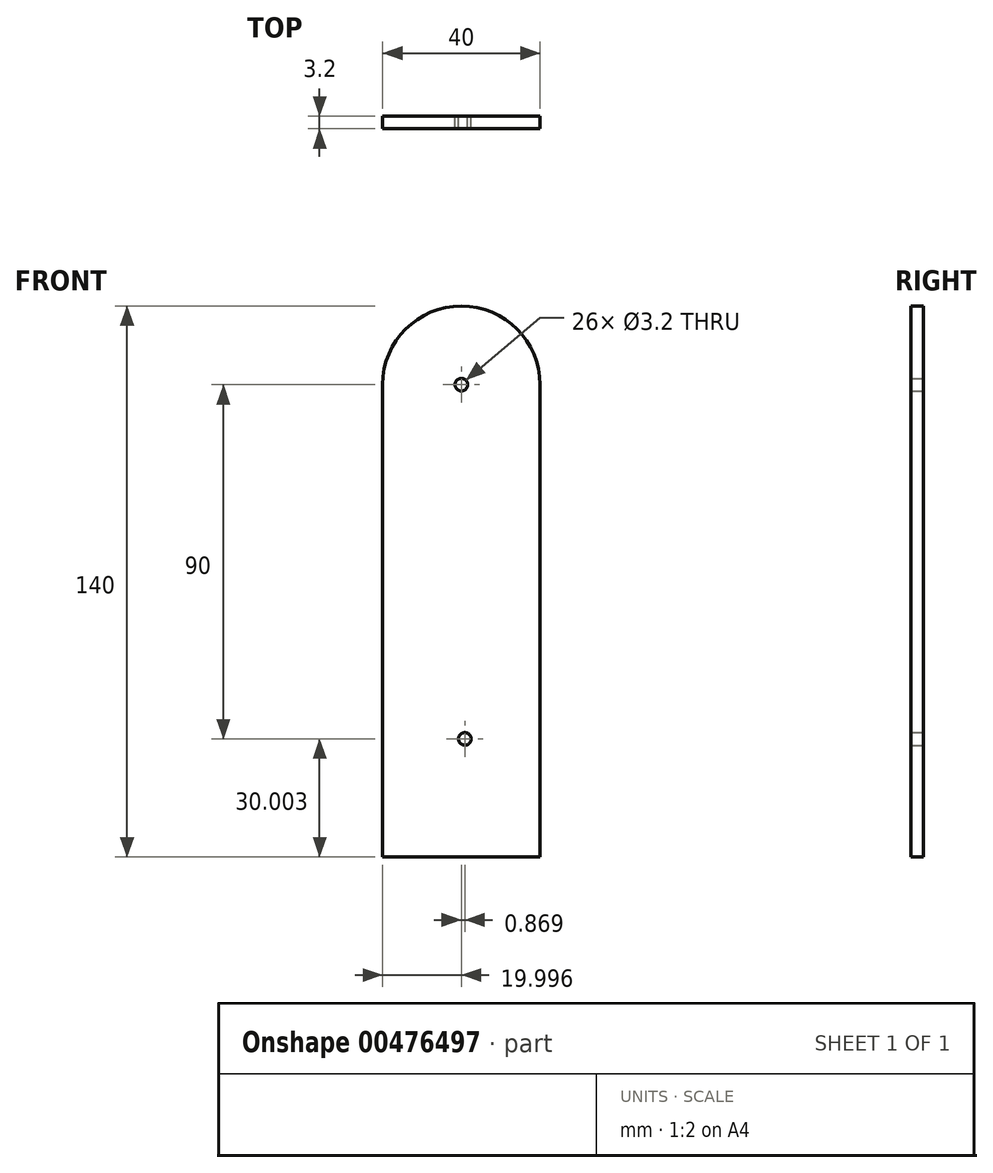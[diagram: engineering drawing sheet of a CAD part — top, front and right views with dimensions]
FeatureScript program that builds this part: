
annotation { "Feature Type Name" : "Feature", "Feature Type Description" : "" }
export const myFeature = defineFeature(function(context is Context, id is Id, definition is map)
    precondition{}
    {
        {
            var Q0;
            Q0=qCreatedBy(makeId("Front.planeOp"),FACE);
            var sketch = newSketch(context, id + "F0", { "sketchPlane" : qUnion([Q0])});
            skLineSegment(sketch, "E0", {"start": v(-9.25, -67.8) * mm, "end": v(-49.25, -67.8) * mm});
            skLineSegment(sketch, "E1", {"start": v(-49.25, -67.8) * mm, "end": v(-49.25, 52.2) * mm});
            skLineSegment(sketch, "E2", {"start": v(-9.25, -67.8) * mm, "end": v(-9.25, 52.2) * mm});
            skPoint(sketch, "E3", {"position": v(23.05, -67.8) * mm});
            skCircle(sketch, "E4", {"center": v(-29.25, 52.2) * mm, "radius": 1.6 * mm});
            skArc(sketch, "E5", {"start": v(-9.25, 52.2) * mm, "mid": v(-29.25, 72.2) * mm, "end": v(-49.25, 52.2) * mm});
            skCircle(sketch, "E6", {"center": v(-28.39, -37.8) * mm, "radius": 1.6 * mm});
            skSolve(sketch);
        }
        {
            var Q0;
            Q0 = qSketchRegion(id + "F0", true);
            extrude(context, id + "F1", {"entities" : qUnion([Q0]), "depth" : 3.2 * mm, "offsetDistance" : 25 * mm});
        }
    });
